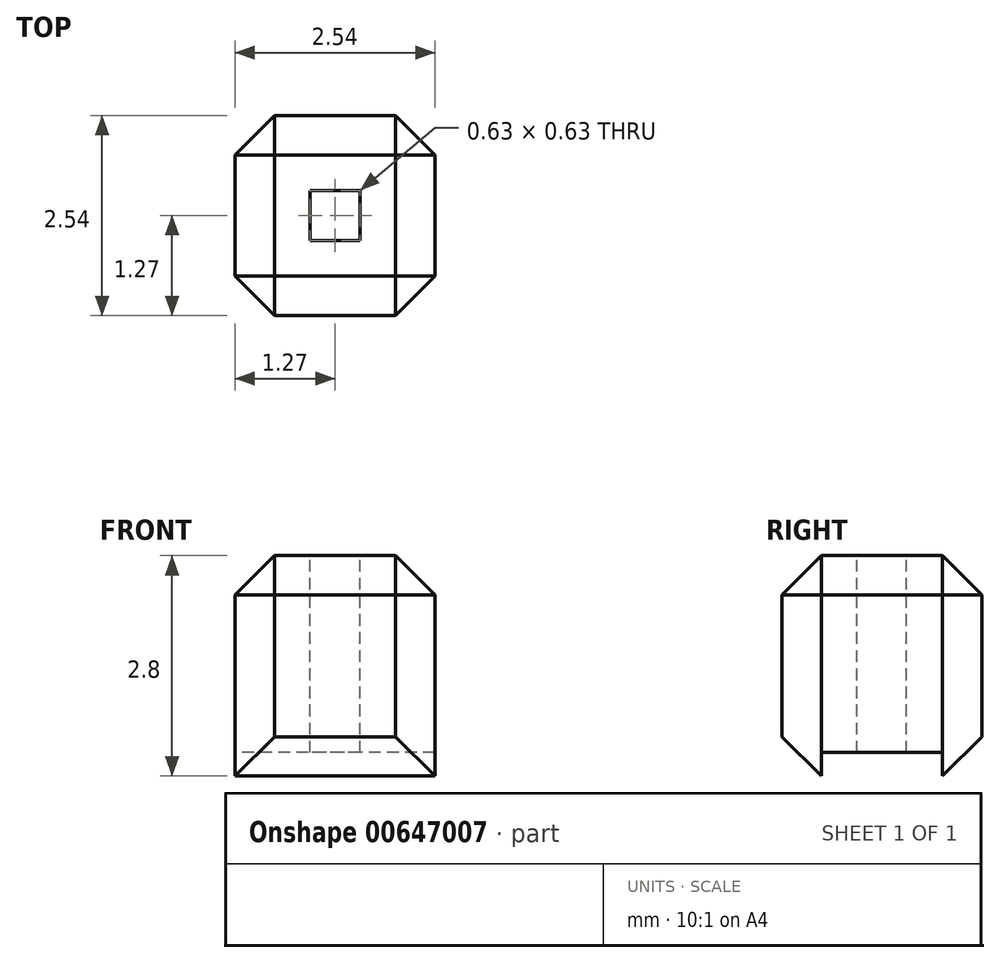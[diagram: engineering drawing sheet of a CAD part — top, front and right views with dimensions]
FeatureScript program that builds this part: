
annotation { "Feature Type Name" : "Feature", "Feature Type Description" : "" }
export const myFeature = defineFeature(function(context is Context, id is Id, definition is map)
    precondition{}
    {
        {
            var Q0;
            Q0=qCreatedBy(makeId("Right.planeOp"),FACE);
            var sketch = newSketch(context, id + "F0", { "sketchPlane" : qUnion([Q0])});
            skLineSegment(sketch, "E0", {"start": v(-1.27, 1.4) * mm, "end": v(1.27, 1.4) * mm});
            skLineSegment(sketch, "E1", {"start": v(1.27, 1.4) * mm, "end": v(1.27, -1.4) * mm});
            skLineSegment(sketch, "E2", {"start": v(1.27, -1.4) * mm, "end": v(0.77, -1.4) * mm});
            skLineSegment(sketch, "E3", {"start": v(0.77, -1.4) * mm, "end": v(0.77, -1.1) * mm});
            skLineSegment(sketch, "E4", {"start": v(0.77, -1.1) * mm, "end": v(-0.77, -1.1) * mm});
            skLineSegment(sketch, "E5", {"start": v(-0.77, -1.1) * mm, "end": v(-0.77, -1.4) * mm});
            skLineSegment(sketch, "E6", {"start": v(-0.77, -1.4) * mm, "end": v(-1.27, -1.4) * mm});
            skLineSegment(sketch, "E7", {"start": v(-1.27, -1.4) * mm, "end": v(-1.27, 1.4) * mm});
            skSolve(sketch);
        }
        {
            var Q0;
            Q0 = qSketchRegion(id + "F0", true);
            extrude(context, id + "F1", {"entities" : qUnion([Q0]), "depth" : 2.54 * mm, "offsetDistance" : 25 * mm});
        }
        {
            var Q0;
            Q0=makeQuery(id+"F1.opExtrude","CAP_EDGE",EDGE,{"disambiguationData":[OSD([sQuery(id+"F0.wireOp",EDGE,"E0")])],"isStart":false});
            var Q1;
            Q1=makeQuery(id+"F1.opExtrude","CAP_EDGE",EDGE,{"disambiguationData":[OSD([sQuery(id+"F0.wireOp",EDGE,"E0")])],"isStart":true});
            var Q2;
            Q2=makeQuery(id+"F1.opExtrude","SWEPT_EDGE",EDGE,{"disambiguationData":[OSD([sQuery(id+"F0.wireOp",EDGE,"E0"),sQuery(id+"F0.wireOp",EDGE,"E7")])]});
            var Q3;
            Q3=makeQuery(id+"F1.opExtrude","SWEPT_EDGE",EDGE,{"disambiguationData":[OSD([sQuery(id+"F0.wireOp",EDGE,"E0"),sQuery(id+"F0.wireOp",EDGE,"E1")])]});
            var Q4;
            Q4=makeQuery(id+"F1.opExtrude","CAP_EDGE",EDGE,{"disambiguationData":[OSD([sQuery(id+"F0.wireOp",EDGE,"E1")])],"isStart":false});
            var Q5;
            Q5=makeQuery(id+"F1.opExtrude","SWEPT_EDGE",EDGE,{"disambiguationData":[OSD([sQuery(id+"F0.wireOp",EDGE,"E1"),sQuery(id+"F0.wireOp",EDGE,"E2")])]});
            var Q6;
            Q6=makeQuery(id+"F1.opExtrude","CAP_EDGE",EDGE,{"disambiguationData":[OSD([sQuery(id+"F0.wireOp",EDGE,"E1")])],"isStart":true});
            var Q7;
            Q7=makeQuery(id+"F1.opExtrude","CAP_EDGE",EDGE,{"disambiguationData":[OSD([sQuery(id+"F0.wireOp",EDGE,"E7")])],"isStart":false});
            var Q8;
            Q8=makeQuery(id+"F1.opExtrude","CAP_EDGE",EDGE,{"disambiguationData":[OSD([sQuery(id+"F0.wireOp",EDGE,"E7")])],"isStart":true});
            var Q9;
            Q9=makeQuery(id+"F1.opExtrude","SWEPT_EDGE",EDGE,{"disambiguationData":[OSD([sQuery(id+"F0.wireOp",EDGE,"E6"),sQuery(id+"F0.wireOp",EDGE,"E7")])]});
            chamfer(context, id + "F2", {"entities" : qUnion([Q0, Q1, Q2, Q3, Q4, Q5, Q6, Q7, Q8, Q9]), "width" : 0.5 * mm, "tangentPropagation" : true});
        }
        {
            var Q0;
            Q0=makeQuery(id+"F1.opExtrude","SWEPT_FACE",FACE,{"disambiguationData":[OSD([sQuery(id+"F0.wireOp",EDGE,"E0")])]});
            var sketch = newSketch(context, id + "F3", { "sketchPlane" : qUnion([Q0])});
            skLineSegment(sketch, "E8.bottom", {"start": v(1.58, -0.32) * mm, "end": v(0.96, -0.32) * mm});
            skLineSegment(sketch, "E8.top", {"start": v(1.58, 0.31) * mm, "end": v(0.95, 0.31) * mm});
            skLineSegment(sketch, "E8.left", {"start": v(1.58, -0.32) * mm, "end": v(1.58, 0.31) * mm});
            skLineSegment(sketch, "E8.right", {"start": v(0.96, -0.32) * mm, "end": v(0.95, 0.31) * mm});
            skPoint(sketch, "E8.middle", {"position": v(1.27, 0) * mm});
            skPoint(sketch, "E8.middle.positionSnap0", {"position": v(1.27, -0.77) * mm});
            skPoint(sketch, "E8.centerSnap0", {"position": v(1.27, -0.77) * mm});
            skSolve(sketch);
        }
        {
            var Q0;
            Q0 = qSketchRegion(id + "F3", true);
            extrude(context, id + "F4", {"entities" : qUnion([Q0]), "operationType" : NewBodyOperationType.REMOVE, "endBound" : BoundingType.UP_TO_NEXT, "oppositeDirection" : true, "depth" : 25 * mm, "offsetDistance" : 25 * mm});
        }
    });
